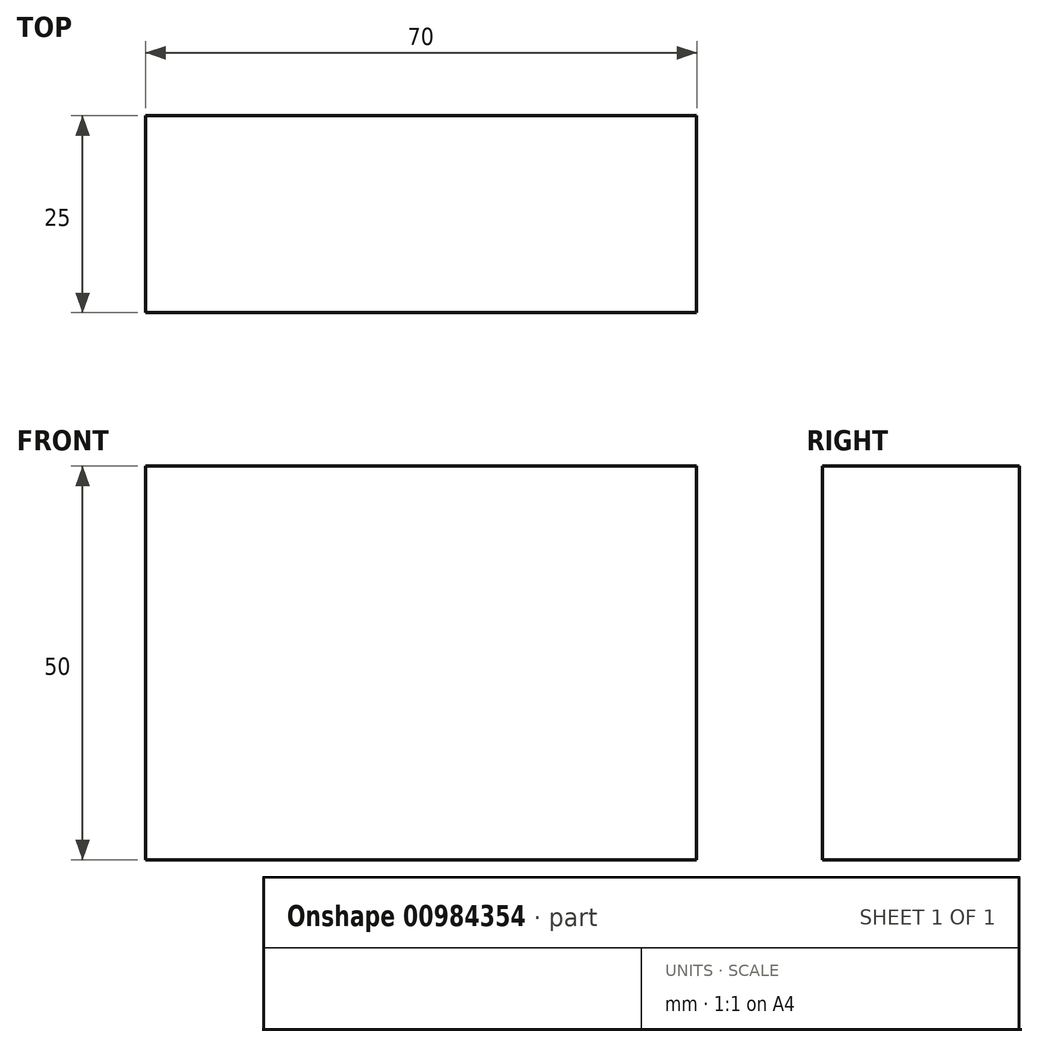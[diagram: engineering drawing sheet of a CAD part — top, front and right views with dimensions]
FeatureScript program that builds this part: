
annotation { "Feature Type Name" : "Feature", "Feature Type Description" : "" }
export const myFeature = defineFeature(function(context is Context, id is Id, definition is map)
    precondition{}
    {
        {
            var Q0;
            Q0=qCreatedBy(makeId("Front.planeOp"),FACE);
            var sketch = newSketch(context, id + "F0", { "sketchPlane" : qUnion([Q0])});
            skLineSegment(sketch, "E0.bottom", {"start": v(-25.97, 28.68) * mm, "end": v(44.03, 28.68) * mm});
            skLineSegment(sketch, "E0.top", {"start": v(-25.97, -21.32) * mm, "end": v(44.03, -21.32) * mm});
            skLineSegment(sketch, "E0.left", {"start": v(-25.97, 28.68) * mm, "end": v(-25.97, -21.32) * mm});
            skLineSegment(sketch, "E0.right", {"start": v(44.03, 28.68) * mm, "end": v(44.03, -21.32) * mm});
            skSolve(sketch);
        }
        {
            var Q0;
            Q0=makeQuery(id+"F0.imprint","IMPRINT",FACE,{"disambiguationData":[TD([[makeQuery(id+"F0.imprint","IMPRINT",EDGE,{"derivedFrom":sQuery(id+"F0.wireOp",EDGE,"E0.bottom")}),-1.0]])]});
            var sketch = newSketch(context, id + "F1", { "sketchPlane" : qUnion([Q0])});
            skSolve(sketch);
        }
        {
            var Q0;
            Q0 = qSketchRegion(id + "F1", true);
            var Q1;
            Q1=makeQuery(id+"F1.imprint","IMPRINT",FACE,{"disambiguationData":[TD([[makeQuery(id+"F1.imprint","IMPRINT",EDGE,{"derivedFrom":makeQuery(id+"F0.imprint","IMPRINT",EDGE,{"derivedFrom":sQuery(id+"F0.wireOp",EDGE,"E0.bottom")})}),-1.0]])]});
            extrude(context, id + "F2", {"entities" : qUnion([Q0, Q1]), "depth" : 25 * mm, "offsetDistance" : 25 * mm});
        }
    });
